FCSTD DOCUMENT  (FreeCAD 0.19R24276 (Git))
Label: Sketch_1
License: All rights reserved
LicenseURL: http://en.wikipedia.org/wiki/All_rights_reserved
objects: Sketcher::SketchObject×1, PartDesign::Body×1
note: 2 computed .brp shape members not serialized (recipe doc carries the construction recipe); baked Part::Feature solids carry a one-line shape summary decoded from their .brp

FEATURE [Sketcher::SketchObject] Sketch
  FullyConstrained = false
  MapMode = 5
  Support = -> [XY_Plane]
  sketch-geometry (18):
    g0: Circle CenterX=0 CenterY=0 CenterZ=0 NormalX=0 NormalY=0 NormalZ=1 AngleXU=0 Radius=45
    g1: ArcOfCircle CenterX=0 CenterY=0 CenterZ=0 NormalX=0 NormalY=0 NormalZ=1 AngleXU=0 Radius=41 StartAngle=1.69256 EndAngle=3.01963
    g2: Circle CenterX=0.00795125 CenterY=41 CenterZ=0 NormalX=0 NormalY=0 NormalZ=1 AngleXU=0 Radius=2.5
    g3: Circle CenterX=41 CenterY=0.00996783 CenterZ=0 NormalX=0 NormalY=0 NormalZ=1 AngleXU=0 Radius=2.5
    g4: Circle CenterX=5.71024e-06 CenterY=-41 CenterZ=0 NormalX=0 NormalY=0 NormalZ=1 AngleXU=0 Radius=2.5
    g5: Circle CenterX=-41 CenterY=-9.93634e-07 CenterZ=0 NormalX=0 NormalY=0 NormalZ=1 AngleXU=0 Radius=2.5
    g6: ArcOfCircle CenterX=-41 CenterY=-9.93634e-07 CenterZ=0 NormalX=0 NormalY=0 NormalZ=1 AngleXU=0 Radius=4.99735 StartAngle=4.77337 EndAngle=7.793
    g7: ArcOfCircle CenterX=5.71024e-06 CenterY=-41 CenterZ=0 NormalX=0 NormalY=0 NormalZ=1 AngleXU=0 Radius=4.99735 StartAngle=0.0609812 EndAngle=3.08061
    g8: ArcOfCircle CenterX=0.00795125 CenterY=41 CenterZ=0 NormalX=0 NormalY=0 NormalZ=1 AngleXU=0 Radius=4.99731 StartAngle=3.20238 EndAngle=6.22201
    g9: ArcOfCircle CenterX=0 CenterY=0 CenterZ=0 NormalX=0 NormalY=0 NormalZ=1 AngleXU=0 Radius=41 StartAngle=0.122204 EndAngle=1.44864
    g10: ArcOfCircle CenterX=0 CenterY=0 CenterZ=0 NormalX=0 NormalY=0 NormalZ=1 AngleXU=0 Radius=41 StartAngle=4.83435 EndAngle=6.16147
    g11: ArcOfCircle CenterX=0 CenterY=0 CenterZ=0 NormalX=0 NormalY=0 NormalZ=1 AngleXU=0 Radius=41 StartAngle=3.26355 EndAngle=4.59043
    g12: ArcOfCircle CenterX=41 CenterY=0.00996783 CenterZ=0 NormalX=0 NormalY=0 NormalZ=1 AngleXU=0 Radius=4.99732 StartAngle=1.63202 EndAngle=4.65165
    g13: LineSegment StartX=0.00795125 StartY=41 StartZ=0 EndX=41 EndY=0.00996783 EndZ=0
    g14: Circle CenterX=0.00795125 CenterY=41 CenterZ=0 NormalX=0 NormalY=0 NormalZ=1 AngleXU=0 Radius=10
    g15: Circle CenterX=41 CenterY=0.00996783 CenterZ=0 NormalX=0 NormalY=0 NormalZ=1 AngleXU=0 Radius=10
    g16: LineSegment StartX=7.252 StartY=47.8938 StartZ=0 EndX=48.0705 EndY=7.08159 EndZ=0
    g17: LineSegment StartX=21.1905 StartY=19.8185 StartZ=0 EndX=32.504 EndY=31.1324 EndZ=0
  constraints (43):
    c: Coincident(g0,g-1)
    c: Diameter(g0) = 90
    c: Coincident(g1,g0)
    c: Diameter(g1) = 82
    c: PointOnObject(g3,g1)
    c: PointOnObject(g5,g1)
    c: PointOnObject(g2,g1)
    c: PointOnObject(g4,g1)
    c: Equal(g5,g4)
    c: Equal(g4,g3)
    c: Equal(g3,g2)
    c: Diameter(g2) = 5
    c: Coincident(g6,g5)
    c: Coincident(g7,g4)
    c: Equal(g6,g7)
    c: Coincident(g1,g8)
    c: Coincident(g9,g8)
    c: Equal(g1,g9)
    c: Coincident(g1,g9)
    c: Equal(g1,g10)
    c: Coincident(g1,g10)
    c: Equal(g1,g11)
    c: Coincident(g1,g11)
    c: Coincident(g12,g10)
    c: Coincident(g12,g9)
    c: Coincident(g7,g10)
    c: Coincident(g7,g11)
    c: Coincident(g6,g11)
    c: Coincident(g6,g1)
    c: Coincident(g12,g3)
    c: Coincident(g8,g2)
    c: Coincident(g13,g2)
    c: Coincident(g13,g3)
    c: Coincident(g14,g2)
    c: Coincident(g15,g3)
    c: Diameter(g14) = 20
    c: Equal(g14,g15)
    c: PointOnObject(g16,g14)
    c: PointOnObject(g16,g15)
    c: Tangent(g16,g15)
    c: PointOnObject(g17,g13)
    c: Angle(g17,g13) = 1.5708
    c: Distance(g17) = 16
FEATURE [PartDesign::Body] Body
  Group = -> [Sketch]
  Origin = -> Origin
